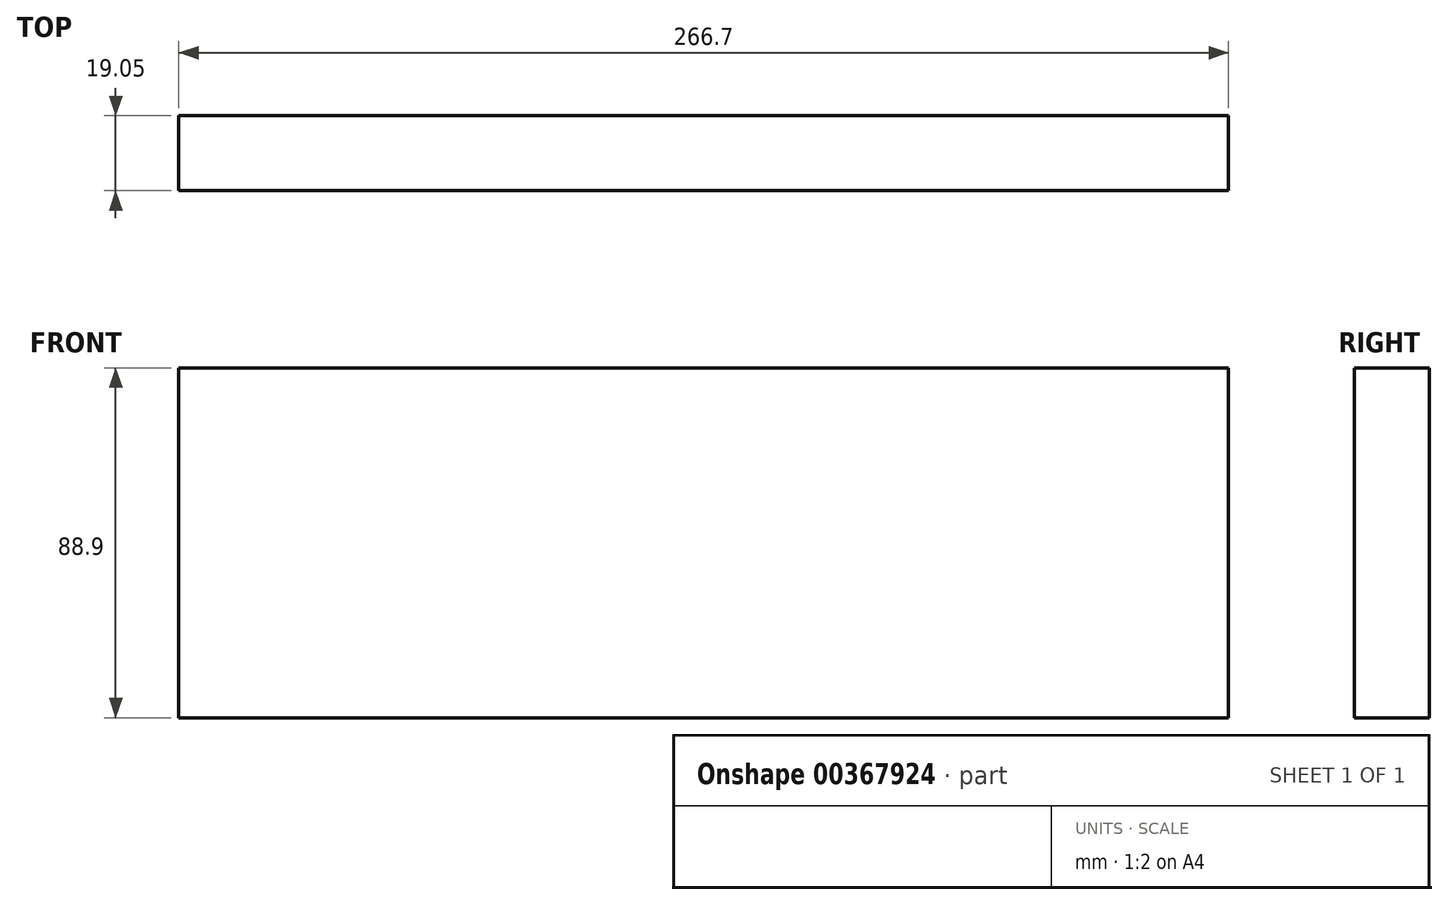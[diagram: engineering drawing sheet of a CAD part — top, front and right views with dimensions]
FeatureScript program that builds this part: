
annotation { "Feature Type Name" : "Feature", "Feature Type Description" : "" }
export const myFeature = defineFeature(function(context is Context, id is Id, definition is map)
    precondition{}
    {
        {
            var Q0;
            Q0=qCreatedBy(makeId("Front.planeOp"),FACE);
            var sketch = newSketch(context, id + "F0", { "sketchPlane" : qUnion([Q0])});
            skLineSegment(sketch, "E0.bottom", {"start": v(-153.24, 91.56) * mm, "end": v(113.46, 91.56) * mm});
            skLineSegment(sketch, "E0.top", {"start": v(-153.24, 2.66) * mm, "end": v(113.46, 2.66) * mm});
            skLineSegment(sketch, "E0.left", {"start": v(-153.24, 91.56) * mm, "end": v(-153.24, 2.66) * mm});
            skLineSegment(sketch, "E0.right", {"start": v(113.46, 91.56) * mm, "end": v(113.46, 2.66) * mm});
            skSolve(sketch);
        }
        {
            var Q0;
            Q0=makeQuery(id+"F0.imprint","IMPRINT",FACE,{"disambiguationData":[TD([[makeQuery(id+"F0.imprint","IMPRINT",EDGE,{"derivedFrom":sQuery(id+"F0.wireOp",EDGE,"E0.bottom")}),-1.0]])]});
            extrude(context, id + "F1", {"entities" : qUnion([Q0]), "depth" : 19.05 * mm});
        }
    });
